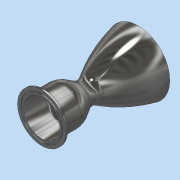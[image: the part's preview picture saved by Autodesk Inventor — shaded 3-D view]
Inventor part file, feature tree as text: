
AUTODESK INVENTOR PART (.ipt)
format: ipt  version: 2020 (Build 240168000, 168)  size: 241,152 bytes
history: native  units: in
note: dims shown in document units (in); Inventor stores cm internally (conversion verified against a paired STEP export)
features: fillet x4, other x2
ambient origin geometry x8: Origin, YZ Plane, XZ Plane, XY Plane, X Axis, Y Axis, Z Axis, Center Point
bodies: Body1 (feature_tree)
feature tree (6):
  other  "CD Nozzle"
  fillet  "Fillet14"  [1 undecoded]
  fillet  "Fillet15"  Radius=1.7717in
  fillet  "Fillet16"  Radius=1.378in
  fillet  "Fillet17"  Radius=0.5906in
  other  "CD Nozzle Sketch"
note: 1 required parameter value undecoded (feature->parameter linkage not recoverable at this tier; creation-order binding heuristic only, values carry confidence <= 0.55)
